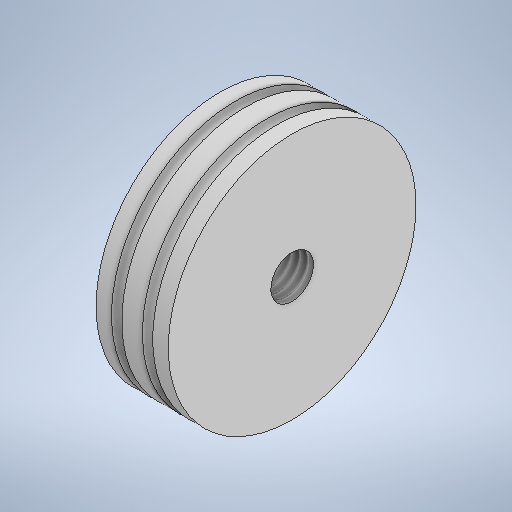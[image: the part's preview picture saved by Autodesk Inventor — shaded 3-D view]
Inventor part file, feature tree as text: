
AUTODESK INVENTOR PART (.ipt)
format: ipt  version: 2025.1 (Build 291241000, 241)  size: 300,032 bytes
history: native  units: mm
features: sketch x3, hole x2, revolve x1
ambient origin geometry x8: Origin, YZ Plane, XZ Plane, XY Plane, X Axis, Y Axis, Z Axis, Center Point
bodies: Solid1 (feature_tree)
feature tree (6):
  revolve  "Revolution1"  [1 undecoded]
  hole  "Hole1"  [1 undecoded]
  hole  "Hole2"  [1 undecoded]
  sketch  "Sketch1"  dims[d0=7.0mm d2=0.5mm]
  sketch  "Sketch2"  dims[d3=0.5mm d4=2.0mm]
  sketch  "Sketch3"  dims[d5=2.0mm d6=24.0mm d7=90.0deg d8=10.0mm d9=6.0mm d10=4.0mm d11=2.0mm d12=90.0deg d13=2.0mm d14=0.0mm d15=4.134mm d16=5.0mm d17=4.0mm d18=2.0mm d19=90.0deg d20=5.0mm d21=0.0mm]
note: 3 required parameter values undecoded (feature->parameter linkage not recoverable at this tier; creation-order binding heuristic only, values carry confidence <= 0.55)